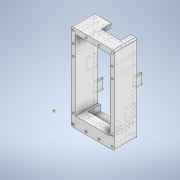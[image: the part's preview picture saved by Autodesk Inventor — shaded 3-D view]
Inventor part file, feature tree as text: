
AUTODESK INVENTOR PART (.ipt)
format: ipt  version: 2022 (Build 260153000, 153)  size: 3,481,088 bytes
history: native  units: in
note: dims shown in document units (in); Inventor stores cm internally (conversion verified against a paired STEP export)
features: sketch x46, extrude x43, fillet x26, other x15, hole x5, chamfer x3, plane x1, split x1
ambient origin geometry x8: Origin, YZ Plane, XZ Plane, XY Plane, X Axis, Y Axis, Z Axis, Center Point
bodies: Body1 (feature_tree), Body2 (feature_tree), Body3 (feature_tree), Body4 (feature_tree), Body5 (feature_tree), Body6 (feature_tree), Body7 (feature_tree), Body8 (feature_tree), Body9 (feature_tree), Body10 (feature_tree), Body11 (feature_tree), Body12 (feature_tree), Body13 (feature_tree)
feature tree (140):
  other  "Faceplate"
  extrude  "Front Panel Blank"  Depth=4.7244in
  hole  "Panel Mount Screw Holes"  [1 undecoded]
  extrude  "Voltmeter Screen"  Depth=0.0984in TaperAngle=0.0deg
  extrude  "Knob Indents"  Depth=0.1181in
  extrude  "Pot Mounting Holes"  Depth=0.1181in
  extrude  "Connector Indents"  Depth=0.1181in
  extrude  "Connector Mounting Holes"  Depth=0.5906in
  fillet  "Fillet1"  Radius=0.5906in
  other  "Work Point1"
  extrude  "Pot Back Keepouts"  Depth=1.1811in
  extrude  "Chassis"  Depth=0.5906in
  extrude  "Display"  Depth=0.1969in
  extrude  "Chassis 2"  Depth=1.7717in
  extrude  "Back Chassis Plate"  Depth=0.4724in
  extrude  "PCB Standoffs"  Depth=0.0197in
  extrude  "PCB"  Depth=0.0197in
  hole  "PCB Screw Mounts"  [1 undecoded]
  extrude  "Heatsinks"  Depth=1.063in
  extrude  "Air Holes 1"  Depth=0.7874in
  fillet  "Fillet2"  Radius=0.9449in
  fillet  "Fillet3"  Radius=0.7874in
  extrude  "Fan Body"  Depth=0.6693in
  extrude  "Top Air Holes"  Depth=0.2756in
  hole  "Hole5"  [1 undecoded]
  fillet  "Fillet11"  Radius=0.5512in
  fillet  "Fillet12"  Radius=0.5512in
  fillet  "Fillet13"  Radius=1.378in
  fillet  "Fillet14"  Radius=0.5906in
  extrude  "Text Labels"  Depth=0.0394in
  extrude  "Logo"  TaperAngle=0.0deg  [1 undecoded]
  fillet  "Fillet15"  Radius=0.5906in
  fillet  "Fillet16"  Radius=0.0787in
  fillet  "Fillet17"  Radius=2.3622in
  fillet  "Fillet18"  Radius=1.1811in
  fillet  "Fillet19"  Radius=0.3937in
  fillet  "Fillet20"  Radius=0.5906in
  fillet  "Fillet21"  Radius=1.9685in
  fillet  "Fillet24"  Radius=0.1181in
  fillet  "Fillet25"  Radius=0.1181in
  fillet  "Fillet26"  Radius=0.1181in
  extrude  "Body 3 Mains Section"  Depth=0.1181in
  extrude  "Transformer Metal"  Depth=0.2362in
  extrude  "Transformer Yellow"  Depth=0.1476in
  extrude  "body3 lid"  Depth=0.2756in
  extrude  "IEC Panelmount"  Depth=0.3346in
  extrude  "IEC inside"  Depth=0.3346in
  extrude  "IEC socket"  Depth=0.3346in
  extrude  "body3 IEC hole"  Depth=0.7087in
  chamfer  "IEPin Sculpting"  Distance=0.3937in
  fillet  "Fillet27"  Radius=0.2756in
  fillet  "Fillet28"  Radius=0.315in
  fillet  "Fillet29"  Radius=0.1181in
  hole  "IEC Screwholes"  [1 undecoded]
  hole  "Faceplate Mounting Holes"  [1 undecoded]
  sketch  "Sketch41"  dims[d153=0.7087in d154=0.7087in]
  extrude  "IEC Pins"  Depth=0.2362in
  chamfer  "Chamfer2"  Distance=0.1181in
  extrude  "Switch Panel Mount"  Depth=0.5906in
  extrude  "Switch Body"  Depth=0.6299in
  extrude  "Switch Switch"  Depth=0.0787in TaperAngle=0.0deg
  extrude  "Switch Carve"  Depth=1.378in TaperAngle=0.0deg
  fillet  "Fillet30"  Radius=0.1181in
  fillet  "Fillet31"  Radius=0.3543in
  extrude  "Extrusion34"  Depth=0.3543in
  chamfer  "Chamfer3"  Distance=0.3543in
  extrude  "Extrusion35"  Depth=0.3543in
  extrude  "Extrusion36"  Depth=1.0236in
  fillet  "Fillet32"  Radius=2.3031in
  extrude  "Extrusion37"  Depth=0.0512in
  extrude  "Extrusion38"  Depth=0.1969in TaperAngle=0.0deg
  extrude  "Extrusion39"  Depth=0.0512in
  extrude  "Extrusion40"  Depth=1.4567in
  fillet  "Fillet33"  Radius=0.128in
  plane  "Work Plane1"
  split  "Split1"
  extrude  "Extrusion41"  Depth=0.0512in
  extrude  "Extrusion42"  Depth=0.0512in
  fillet  "Fillet34"  Radius=0.063in
  extrude  "Extrusion43"  Depth=0.0512in
  extrude  "Extrusion44"  Depth=0.0512in
  fillet  "Fillet35"  Radius=0.1181in
  sketch  "Sketch1"  dims[d0=3.1496in d1=4.7244in]
  sketch  "Sketch2"  dims[d2=2.3622in d4=1.5748in]
  sketch  "Sketch3"  dims[d5=0.3937in d6=0.0984in d7=0.0in]
  sketch  "Sketch4"  dims[d8=0.1181in d9=0.1181in]
  sketch  "Sketch5"  dims[d10=0.1181in d11=0.1181in]
  sketch  "Sketch6"  dims[d12=0.1181in d13=0.1181in]
  sketch  "Sketch7"  dims[d14=0.1181in d15=0.1181in d16=0.5906in]
  other  "Body 1"
  sketch  "Sketch11"  dims[d17=0.5906in d18=1.1811in]
  sketch  "Sketch14"  dims[d19=0.5906in d20=0.5906in]
  other  "Pots"
  sketch  "Sketch15"  dims[d21=0.1969in d22=0.1969in]
  other  "Screen"
  sketch  "Sketch16"  dims[d23=0.126in d24=0.2362in d25=0.248in d26=0.0787in d27=90.0deg d28=0.315in d29=0.8108in d30=1.7717in]
  other  "Body 2"
  sketch  "Sketch17"  dims[d31=0.5906in d32=1.0236in d33=0.8858in d34=0.9449in d35=0.4724in]
  sketch  "Sketch18"  dims[d36=0.0197in d37=0.0197in d38=0.0197in]
  other  "Power Module"
  sketch  "Sketch20"  dims[d39=0.0197in d40=0.9449in]
  sketch  "Sketch21"  dims[d42=0.5906in d43=1.0236in]
  other  "Power Moudle Heat Sinks"
  sketch  "Sketch22"  dims[d44=0.4724in d45=1.063in]
  sketch  "Sketch24"  dims[d46=0.1969in d47=0.0in d48=0.9449in d49=0.9449in d50=0.7874in]
  other  "Cooling_fan"
  sketch  "Sketch25"  dims[d51=0.6693in d52=0.6693in]
  sketch  "Sketch26"  dims[d53=0.0394in d54=0.0in d55=0.2756in]
  sketch  "Sketch28"  dims[d56=0.2756in d57=0.0394in d58=0.0in d59=0.5512in d60=0.5512in d61=1.378in d64=0.5906in]
  sketch  "Sketch30"  dims[d65=0.0394in d66=0.0in d67=0.187in]
  other  "Body 3"
  sketch  "Sketch31"  dims[d68=0.187in d69=0.0in d70=0.0in d71=0.5906in d72=0.0787in d81=2.3622in d82=1.1811in d85=0.3937in d86=0.2756in d87=0.5906in d88=0.0in d91=1.9685in d99=0.1181in d100=0.1181in d101=0.1181in]
  other  "Transformer"
  sketch  "Sketch32"  dims[d102=0.1181in d103=0.1181in]
  sketch  "Sketch33"  dims[d104=0.2362in d105=0.2362in]
  sketch  "Sketch34"  dims[d106=0.1181in d109=0.1476in]
  other  "IEC"
  sketch  "Sketch35"  dims[d110=0.2756in d111=0.128in]
  sketch  "Sketch36"  dims[d147=0.6693in d148=0.3346in]
  sketch  "Sketch37"  dims[d149=0.6693in d150=0.3346in]
  sketch  "Sketch39"  dims[d151=0.3346in d152=0.3346in]
  sketch  "Sketch42"  dims[d155=0.748in]
  sketch  "Sketch43"  dims[d156=0.748in d157=0.3937in d158=0.0in d160=0.2756in d161=0.315in d164=0.1181in]
  other  "Power Switch"
  sketch  "Sketch44"  dims[d165=1.1811in d166=0.1181in]
  sketch  "Sketch45"  dims[d167=0.315in d168=0.315in]
  sketch  "Sketch46"  dims[d169=0.2362in d170=0.2362in]
  sketch  "Sketch47"  dims[d171=2.7559in]
  sketch  "Sketch48"  dims[d172=1.1811in]
  sketch  "Sketch49"  dims[d173=0.6693in]
  sketch  "Sketch50"  dims[d174=0.2756in]
  sketch  "Sketch51"  dims[d175=0.1181in]
  sketch  "Sketch52"  dims[d176=0.1181in]
  sketch  "Sketch53"  dims[d177=0.1181in]
  sketch  "Sketch54"  dims[d178=0.1181in]
  sketch  "Sketch55"  dims[d179=0.1181in]
  sketch  "Sketch57"  dims[d180=0.1181in]
  sketch  "Sketch58"  dims[d181=0.1181in d182=0.1181in d183=0.1476in d185=0.5906in d186=0.6299in d187=0.0968in d188=0.2362in d189=0.248in d190=0.0787in d191=90.0deg d192=1.4961in d193=0.8108in d194=0.0787in d195=0.6693in d196=0.0in d197=0.0in d216=1.378in d217=0.0in d218=0.1181in d219=0.0in d220=0.3543in d221=0.3543in d222=0.3543in d223=0.3543in d224=1.0236in d225=2.3031in d226=0.5118in d230=0.1969in d231=0.0in d232=2.5591in d233=1.4567in d234=0.128in d235=0.0886in d236=0.7283in d237=0.063in d238=0.0in d239=0.1181in d240=0.1181in d241=0.1181in d242=0.1181in d243=0.0968in d244=0.2362in d245=0.248in d246=0.0787in d247=90.0deg d248=0.315in d249=0.8108in d250=0.0394in d251=0.1575in d252=0.1575in d253=0.0394in d254=0.0394in d255=0.1575in d256=0.0394in d257=0.1575in d258=0.0394in d259=0.1575in d260=0.0394in d261=0.1575in d262=0.0394in d263=0.1575in d264=0.0394in d265=0.1575in d266=0.0394in d267=0.1575in d268=0.0394in d269=1.811in d270=0.0906in d271=0.3937in d272=0.0906in d274=0.374in d275=0.374in d276=0.8268in d277=0.0in d278=0.1969in d288=1.9685in d289=1.5748in d290=1.1811in d295=0.6693in d296=1.122in d304=0.0984in d305=0.0984in d306=0.0984in d307=0.0984in d308=0.0984in d309=0.0984in d310=0.0984in d311=0.0984in d312=0.0984in d313=0.1181in d314=0.1181in d315=0.1181in d316=0.1181in d317=0.1181in d318=0.1181in d319=0.1181in d320=0.1181in d321=0.315in d322=0.1969in d323=0.0in d324=0.0in d326=0.0689in d327=0.0689in d353=0.3937in d354=0.0in d355=0.0394in d356=0.0787in d357=1.1811in d358=1.1811in d359=0.0787in d360=0.0787in d361=0.0787in d362=0.0787in d363=0.9449in d364=0.9449in d365=0.1181in d366=0.1181in d367=0.1181in d368=0.1181in d375=0.5512in d376=0.0in d377=1.1024in d378=0.5906in d379=0.5906in d380=0.7283in d381=0.0787in d382=0.0787in d383=0.0787in d384=0.0394in d385=0.0394in d386=0.0394in d387=0.0787in d388=0.0787in d389=0.3642in d390=0.5512in d391=0.3642in d392=0.5512in d393=0.3642in d394=0.5512in d395=0.3642in d396=0.5512in d397=0.0787in d398=0.0787in d399=0.0408in d400=0.1877in d401=0.0408in d402=0.0408in d403=0.5906in d404=0.5906in d405=0.0787in d406=0.1181in d441=0.0787in d442=0.0787in d443=0.0787in d444=0.0787in d445=0.0617in d446=0.1575in d447=0.119in d448=0.188in d449=0.5635in d450=0.248in d451=0.0in d452=0.0787in d453=0.0787in d454=0.0394in d455=0.0394in d456=0.1181in d457=0.1181in d459=0.5118in d460=0.2362in d461=0.7087in d463=0.7087in d464=0.7087in d465=0.0787in d466=0.0787in d468=0.4134in d471=1.3386in d472=0.1969in d473=0.5709in d476=0.0787in d477=0.0in d479=0.0787in d480=0.0in d481=0.0in d488=0.0in d489=0.0in d490=0.7382in d491=0.1772in d492=0.1772in d493=0.7382in d494=0.1772in d495=0.1772in d496=0.1772in d497=0.1772in d498=0.5512in d499=0.5512in d500=0.5512in d501=0.6693in d502=0.3642in d503=0.3642in d504=0.187in d505=0.187in d506=0.0984in d507=0.0984in d508=0.0787in d509=0.0787in d510=0.0787in d511=0.0394in d512=0.0118in d513=4.7244in d514=2.3622in d515=0.0in d518=0.0551in d519=0.0551in d520=0.0551in d521=1.5945in d532=0.5512in d533=1.2205in d534=1.8976in d535=0.0in d536=1.2598in d537=1.1417in d538=0.2264in d539=0.2264in d540=0.3189in d541=0.3189in d542=0.5118in d543=1.6614in d544=0.0in d545=0.0in d546=0.1181in d547=0.0in d549=1.3012in d552=0.6506in d553=1.124in d554=0.3268in d555=0.6506in d556=0.6506in d557=0.3268in d558=0.1969in d559=0.0in d560=1.2205in d561=1.063in d562=0.0394in d564=0.0305in d566=0.5512in d567=0.9843in d568=0.9843in d570=0.2559in d571=0.2362in d572=0.0305in d573=0.2559in d574=0.689in d575=0.0in d576=0.9567in d577=0.6535in d578=0.1205in d579=0.0837in d580=0.0837in d581=0.5402in d582=0.2083in d583=0.2083in d585=0.1969in d586=0.0787in d587=0.0787in d588=0.0787in d589=0.1575in d590=0.1575in d591=0.1575in d592=0.1575in d593=0.3307in d594=0.439in d595=0.439in d596=0.1575in d597=0.1575in d598=0.689in d599=0.0in d600=0.689in d601=0.0in d602=0.0394in d603=0.0787in d604=45.0deg d605=0.1969in d606=0.1181in d607=0.1181in d608=0.2247in d609=0.2247in d611=1.437in d612=0.2402in d613=0.2402in d614=0.6496in d615=0.0968in d616=0.2362in d617=0.1575in d618=0.0787in d619=90.0deg d620=0.315in d621=0.8108in d622=0.9449in d623=0.0394in d624=1.7776in d625=0.3268in d631=1.6772in d632=1.6772in d633=1.1417in d634=1.0236in d638=0.063in d639=0.063in d640=0.063in d641=0.0787in d642=0.1181in d643=0.3937in d644=0.2559in d645=0.2559in d646=0.2559in d647=0.1693in d648=0.5906in d649=1.1024in d650=0.4724in d651=0.0in d652=0.0197in d653=0.0787in d654=45.0deg d655=0.2756in d656=0.2756in d657=0.2362in d658=0.2362in d659=0.1476in d660=0.1476in d661=1.1811in d662=0.9843in d663=0.0787in d664=0.0in d665=0.8528in d666=1.0669in d667=0.0571in d668=0.0571in d669=0.0657in d670=0.0657in d671=0.7087in d672=0.0in d673=0.1063in d674=0.1063in d675=0.1063in d676=0.1063in d677=0.2756in d678=0.0in d679=0.1575in d680=0.0394in d681=1.378in d682=0.3937in d683=0.0079in d684=0.2756in d685=0.0in d686=0.0197in d687=0.0118in d688=0.0394in d689=0.2953in d690=0.0394in d691=0.1181in d692=0.8528in d693=0.4264in d694=0.315in d695=0.4067in d696=0.4067in d697=0.0315in d698=0.0315in d699=0.248in d700=0.248in d701=0.1732in d702=0.1772in d704=0.0787in d705=0.0787in d706=0.0591in d707=0.0591in d708=0.0591in d709=0.0591in d710=0.0394in d711=0.0394in d712=0.0394in d713=0.0394in d714=0.2953in d715=0.4067in d716=0.1732in d717=0.1772in d718=0.0787in d719=0.0787in d720=0.4331in d721=0.0in d722=0.0394in d723=0.0787in d724=45.0deg d725=0.4331in d726=0.0in d727=0.0591in d728=0.0591in d729=0.0591in d730=0.0591in d731=0.1969in d732=0.0in d733=0.0787in d734=0.0in d735=0.1969in d736=0.0in d737=0.0in d738=0.5512in d739=0.5906in d740=0.1181in d741=0.1181in d742=0.1181in d743=0.1181in d744=0.0in d745=0.0in d746=0.2165in d747=0.2165in d748=0.2165in d749=0.2165in d750=1.2598in d751=0.0in d752=0.1181in d753=0.1181in d754=0.3937in d755=0.3937in d756=0.1181in d757=0.1181in d758=1.2598in d759=0.0in d760=0.0787in d764=0.3937in d765=0.3937in d766=0.1181in d767=0.1181in d768=0.1181in d769=0.1181in d770=0.0669in d771=0.0669in d772=0.1024in d773=0.5906in d774=0.3937in d775=1.5748in d776=0.5906in d777=0.0669in d778=0.0669in d779=0.3937in d780=0.0in d781=0.4724in d782=0.0in d783=0.0512in d784=0.063in d786=0.063in d788=0.0079in d789=0.063in d790=0.063in d791=0.0079in d792=0.0079in d793=0.0079in d794=0.063in d795=0.063in d796=0.063in d797=0.063in d798=0.4724in d799=0.0in d800=0.5906in d801=0.3937in d802=0.0669in d803=0.0669in d804=0.0669in d805=0.0669in d806=0.5906in d807=2.1654in d808=0.3937in d809=0.0in d810=0.0512in]
  other  "Body 3 A"
  other  "Body 3 B"
note: 6 required parameter values undecoded (feature->parameter linkage not recoverable at this tier; creation-order binding heuristic only, values carry confidence <= 0.55)
